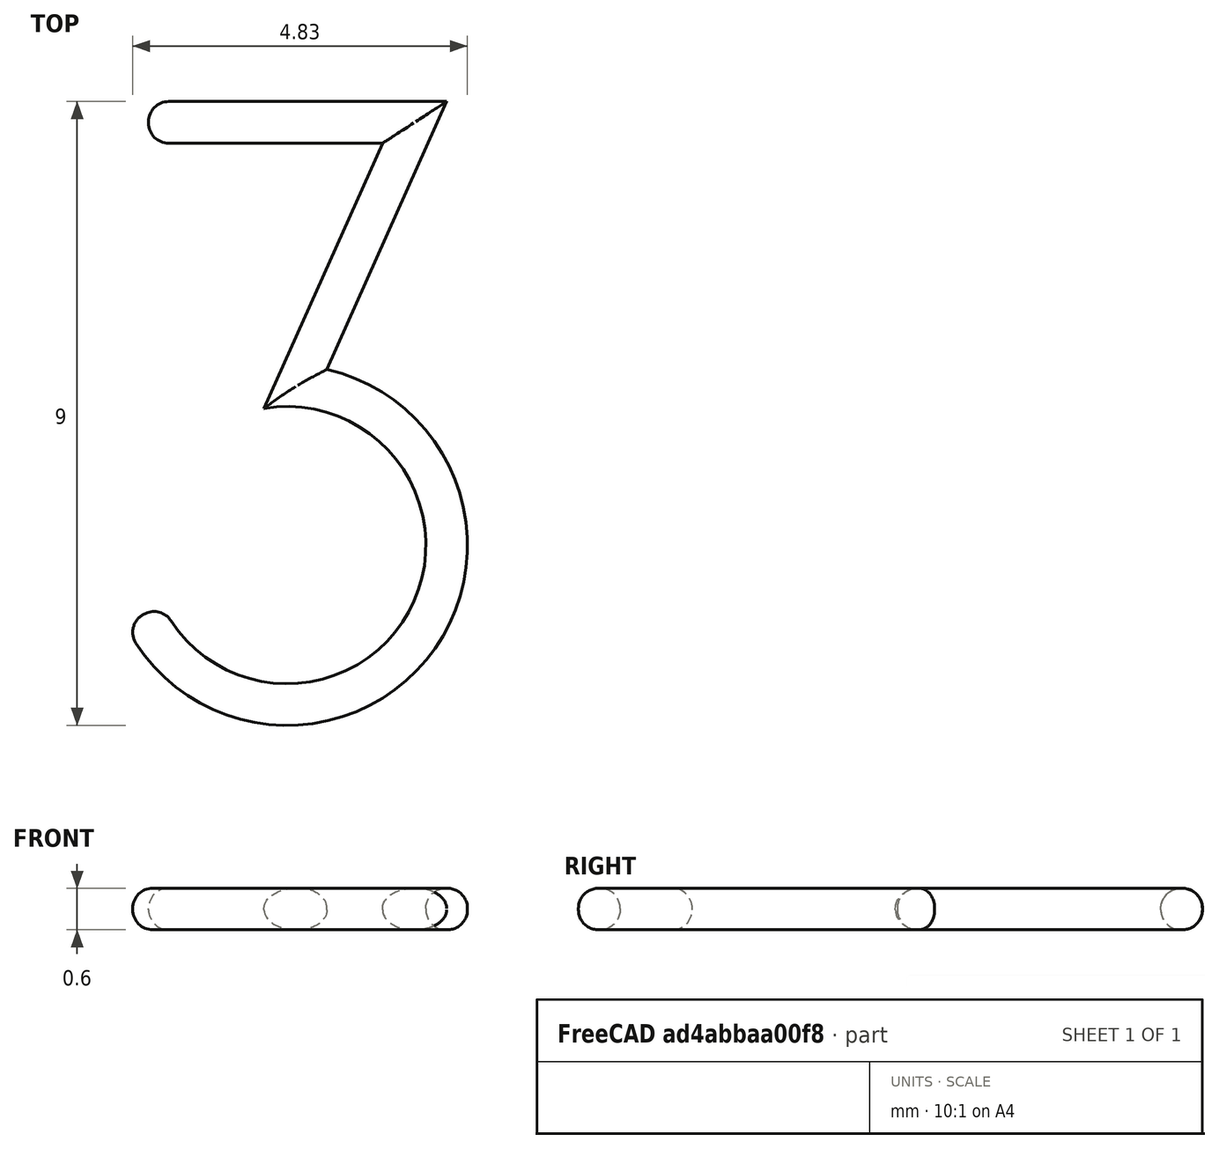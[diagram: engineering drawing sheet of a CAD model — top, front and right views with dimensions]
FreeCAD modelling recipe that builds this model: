
FCSTD DOCUMENT  (FreeCAD 0.16R6712 (Git))
Label: 3s
License: All rights reserved
LicenseURL: http://en.wikipedia.org/wiki/All_rights_reserved
objects: Sketcher::SketchObject×1, PartDesign::Pad×1, PartDesign::Fillet×1, Mesh::Feature×1
note: 4 computed .brp shape members not serialized (recipe doc carries the construction recipe); baked Part::Feature solids carry a one-line shape summary decoded from their .brp

FEATURE [Sketcher::SketchObject] Sketch
  sketch-geometry (8):
    g0: ArcOfCircle CenterX=0 CenterY=2.6 CenterZ=0 NormalX=0 NormalY=0 NormalZ=1 Radius=2 StartAngle=3.59105 EndAngle=8.02236
    g1: LineSegment StartX=-1.80137 StartY=1.73105 StartZ=0 EndX=-2.34178 EndY=1.47037 EndZ=0
    g2: ArcOfCircle CenterX=0 CenterY=2.6 CenterZ=0 NormalX=0 NormalY=0 NormalZ=1 Radius=2.6 StartAngle=3.59105 EndAngle=7.6314
    g3: LineSegment StartX=-2 StartY=9 StartZ=0 EndX=2.3 EndY=9 EndZ=0
    g4: LineSegment StartX=-2 StartY=9 StartZ=0 EndX=-2 EndY=8.4 EndZ=0
    g5: LineSegment StartX=-2 StartY=8.4 StartZ=0 EndX=1.37485 EndY=8.4 EndZ=0
    g6: LineSegment StartX=1.37485 StartY=8.4 StartZ=0 EndX=-0.335173 EndY=4.57171 EndZ=0
    g7: LineSegment StartX=2.3 StartY=9 StartZ=0 EndX=0.573957 EndY=5.13586 EndZ=0
  constraints (23):
    c: Coincident(g1,g0)
    c: Perpendicular(g0,g1)
    c: Distance(g0,g1) = 0.6
    c: PointOnObject(g0,g-2)
    c: Coincident(g2,g0)
    c: Coincident(g2,g1)
    c: Tangent(g-1,g2)
    c: Horizontal(g3)
    c: Coincident(g4,g3)
    c: Vertical(g4)
    c: Horizontal(g5)
    c: Distance(g4,g3) = 0.6
    c: DistanceY(g-1,g3) = 9
    c: Coincident(g5,g4)
    c: Coincident(g6,g5)
    c: DistanceX(g-2,g3) = -2
    c: DistanceX(g-2,g3) = 2.3
    c: Coincident(g7,g3)
    c: Coincident(g2,g7)
    c: Coincident(g0,g6)
    c: Distance(g2,g6) = 0.6
    c: Radius(g2) = 2.6
    c: Parallel(g6,g7)
FEATURE [PartDesign::Pad] Pad
  Length = 0.6
  Length2 = 100
  Midplane = true
  Sketch = -> Sketch
  Type = 0
FEATURE [PartDesign::Fillet] Fillet
  Base = -> Pad [Edge1,Edge20,Edge23,Edge24,Edge4,Edge7,Edge10,Edge13,Edge16,Edge19,Edge22,Edge11,Edge8,Edge12,Edge3,Edge6,Edge9,Edge15,Edge18,Edge21]
  Radius = 0.29
FEATURE [Mesh::Feature] Mesh  label="Fillet (Meshed)"
